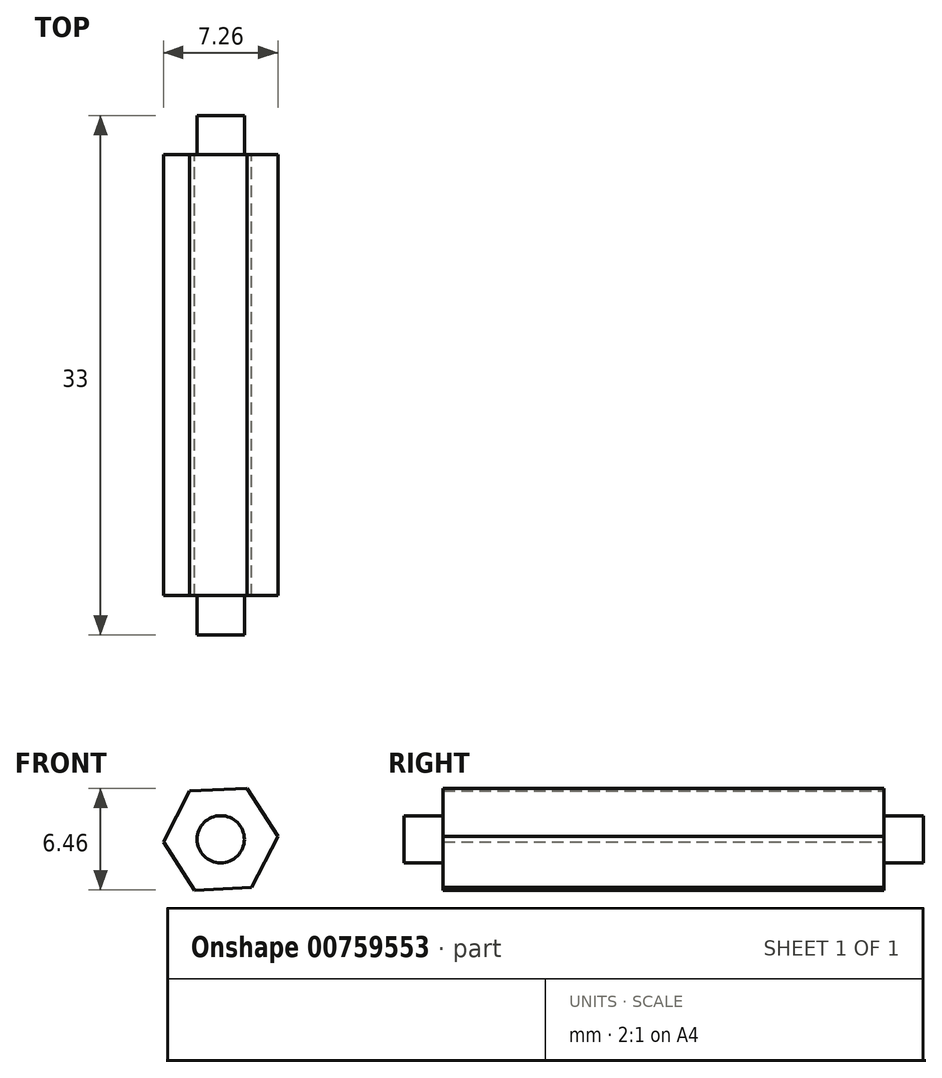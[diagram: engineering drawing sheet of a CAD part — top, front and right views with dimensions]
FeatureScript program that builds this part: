
annotation { "Feature Type Name" : "Feature", "Feature Type Description" : "" }
export const myFeature = defineFeature(function(context is Context, id is Id, definition is map)
    precondition{}
    {
        {
            var Q0;
            Q0=qCreatedBy(makeId("Front.planeOp"),FACE);
            var sketch = newSketch(context, id + "F0", { "sketchPlane" : qUnion([Q0])});
            skCircle(sketch, "E0.cCircle", {"center": v(0, 0) * mm, "radius": 3.15 * mm, "construction": true});
            skLineSegment(sketch, "E0.0", {"start": v(1.67, 3.23) * mm, "end": v(3.63, 0.17) * mm});
            skLineSegment(sketch, "E0.1", {"start": v(3.63, 0.17) * mm, "end": v(1.96, -3.06) * mm});
            skLineSegment(sketch, "E0.2", {"start": v(1.96, -3.06) * mm, "end": v(-1.67, -3.23) * mm});
            skLineSegment(sketch, "E0.3", {"start": v(-1.67, -3.23) * mm, "end": v(-3.63, -0.17) * mm});
            skLineSegment(sketch, "E0.4", {"start": v(-3.63, -0.17) * mm, "end": v(-1.96, 3.06) * mm});
            skLineSegment(sketch, "E0.5", {"start": v(-1.96, 3.06) * mm, "end": v(1.67, 3.23) * mm});
            skPoint(sketch, "E0.0.midPoint", {"position": v(2.65, 1.7) * mm});
            skSolve(sketch);
        }
        {
            var Q0;
            Q0 = qSketchRegion(id + "F0", true);
            extrude(context, id + "F1", {"entities" : qUnion([Q0]), "depth" : 28 * mm, "offsetDistance" : 25 * mm});
        }
        {
            var Q0;
            Q0=makeQuery(id+"F1.opExtrude","CAP_FACE",FACE,{"disambiguationData":[OSD([sQuery(id+"F0.wireOp",EDGE,"E0.0"),sQuery(id+"F0.wireOp",EDGE,"E0.1"),sQuery(id+"F0.wireOp",EDGE,"E0.2"),sQuery(id+"F0.wireOp",EDGE,"E0.3"),sQuery(id+"F0.wireOp",EDGE,"E0.4"),sQuery(id+"F0.wireOp",EDGE,"E0.5")])],"isStart":false});
            var sketch = newSketch(context, id + "F2", { "sketchPlane" : qUnion([Q0])});
            skCircle(sketch, "E1", {"center": v(0, 0) * mm, "radius": 1.5 * mm});
            skSolve(sketch);
        }
        {
            var Q0;
            Q0 = qSketchRegion(id + "F2", true);
            extrude(context, id + "F3", {"entities" : qUnion([Q0]), "operationType" : NewBodyOperationType.ADD, "depth" : 2.5 * mm, "offsetDistance" : 25 * mm});
        }
        {
            var Q0;
            Q0=makeQuery(id+"F1.opExtrude","CAP_FACE",FACE,{"disambiguationData":[OSD([sQuery(id+"F0.wireOp",EDGE,"E0.0"),sQuery(id+"F0.wireOp",EDGE,"E0.1"),sQuery(id+"F0.wireOp",EDGE,"E0.2"),sQuery(id+"F0.wireOp",EDGE,"E0.3"),sQuery(id+"F0.wireOp",EDGE,"E0.4"),sQuery(id+"F0.wireOp",EDGE,"E0.5")])],"isStart":true});
            var sketch = newSketch(context, id + "F4", { "sketchPlane" : qUnion([Q0])});
            skCircle(sketch, "E2", {"center": v(0, 0) * mm, "radius": 1.5 * mm});
            skSolve(sketch);
        }
        {
            var Q0;
            Q0 = qSketchRegion(id + "F4", true);
            extrude(context, id + "F5", {"entities" : qUnion([Q0]), "operationType" : NewBodyOperationType.ADD, "depth" : 2.5 * mm, "offsetDistance" : 25 * mm});
        }
    });
